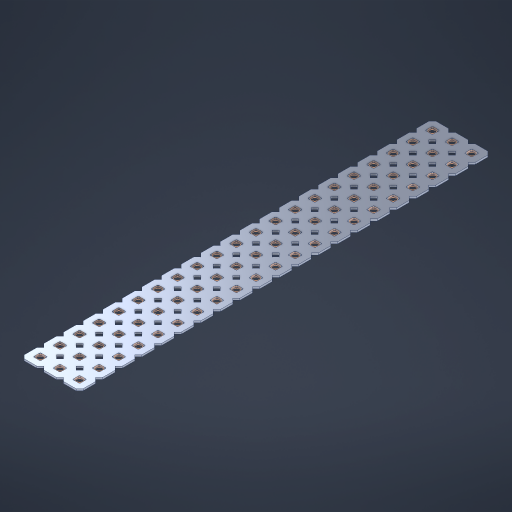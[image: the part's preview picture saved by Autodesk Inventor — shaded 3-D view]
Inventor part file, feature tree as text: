
AUTODESK INVENTOR PART (.ipt)
format: ipt  version: 2023 (Build 270158000, 158)  size: 988,160 bytes
history: native  units: in
note: dims shown in document units (in); Inventor stores cm internally (conversion verified against a paired STEP export)
features: other x64, extrude x62, sketch x2, pattern_linear x1
ambient origin geometry x8: Origin, YZ Plane, XZ Plane, XY Plane, X Axis, Y Axis, Z Axis, Center Point
bodies: Solid1 (feature_tree), Body (feature_tree)
feature tree (129):
  pattern_linear  "Rectangular Pattern1"  Spacing1=0.09in  [1 undecoded]
  sketch  "Sketch1"  dims[d1=0.5in]
  sketch  "Sketch2"  dims[d2=0.182in d3=0.09in d4=0.09in d5=0.09in d6=0.09in d7=0.09in d8=0.09in d9=0.09in d10=0.09in d11=0.02in d13=0.0in d14=0.172in d15=0.0625in d16=0.0in d19=0.5in d22=0.5in]
  other  "Srf1"
  other  "Srf126"
  other  "Srf127"
  other  "Srf128"
  other  "Srf129"
  other  "Srf130"
  other  "Srf131"
  other  "Srf250"
  other  "Srf251"
  other  "Srf252"
  other  "Srf253"
  other  "Srf254"
  other  "Srf255"
  other  "Srf256"
  other  "Srf257"
  other  "Srf258"
  other  "Srf259"
  other  "Srf260"
  other  "Srf261"
  other  "Srf262"
  other  "Srf263"
  other  "Srf268"
  other  "Srf269"
  other  "Srf270"
  other  "Srf271"
  other  "Srf272"
  other  "Srf273"
  other  "Srf274"
  other  "Srf275"
  other  "Srf276"
  other  "Srf277"
  other  "Srf278"
  other  "Srf279"
  other  "Srf280"
  other  "Srf281"
  other  "Srf282"
  other  "Srf283"
  other  "Srf284"
  other  "Srf285"
  other  "Srf286"
  other  "Srf287"
  other  "Srf288"
  other  "Srf293"
  other  "Srf294"
  other  "Srf295"
  other  "Srf296"
  other  "Srf297"
  other  "Srf298"
  other  "Srf299"
  other  "Srf300"
  other  "Srf301"
  other  "Srf302"
  other  "Srf303"
  other  "Srf304"
  other  "Srf305"
  other  "Srf306"
  other  "Srf307"
  other  "Srf308"
  other  "Srf309"
  other  "Srf310"
  other  "Srf311"
  other  "Srf312"
  other  "Srf313"
  other  "Circle"
  extrude  "ExtrusionSrf126"  Depth=0.09in
  extrude  "ExtrusionSrf127"  Depth=0.09in
  extrude  "ExtrusionSrf128"  Depth=0.09in
  extrude  "ExtrusionSrf129"  Depth=0.09in
  extrude  "ExtrusionSrf130"  Depth=0.09in
  extrude  "ExtrusionSrf131"  Depth=0.09in
  extrude  "ExtrusionSrf250"  Depth=0.09in
  extrude  "ExtrusionSrf251"  Depth=0.02in
  extrude  "ExtrusionSrf252"  TaperAngle=0.0deg  [1 undecoded]
  extrude  "ExtrusionSrf253"  Depth=0.5in
  extrude  "ExtrusionSrf254"  Depth=0.5in TaperAngle=0.0deg
  extrude  "ExtrusionSrf255"  Depth=0.5in
  extrude  "ExtrusionSrf256"  Depth=0.5in
  extrude  "ExtrusionSrf257"  [1 undecoded]
  extrude  "ExtrusionSrf258"  [1 undecoded]
  extrude  "ExtrusionSrf259"  [1 undecoded]
  extrude  "ExtrusionSrf260"  [1 undecoded]
  extrude  "ExtrusionSrf261"  [1 undecoded]
  extrude  "ExtrusionSrf262"  [1 undecoded]
  extrude  "ExtrusionSrf263"  [1 undecoded]
  extrude  "ExtrusionSrf268"  [1 undecoded]
  extrude  "ExtrusionSrf269"  [1 undecoded]
  extrude  "ExtrusionSrf270"  [1 undecoded]
  extrude  "ExtrusionSrf271"  [1 undecoded]
  extrude  "ExtrusionSrf272"  [1 undecoded]
  extrude  "ExtrusionSrf273"  [1 undecoded]
  extrude  "ExtrusionSrf274"  [1 undecoded]
  extrude  "ExtrusionSrf275"  [1 undecoded]
  extrude  "ExtrusionSrf276"  [1 undecoded]
  extrude  "ExtrusionSrf277"  [1 undecoded]
  extrude  "ExtrusionSrf278"  [1 undecoded]
  extrude  "ExtrusionSrf279"  [1 undecoded]
  extrude  "ExtrusionSrf280"  [1 undecoded]
  extrude  "ExtrusionSrf281"  [1 undecoded]
  extrude  "ExtrusionSrf282"  [1 undecoded]
  extrude  "ExtrusionSrf283"  [1 undecoded]
  extrude  "ExtrusionSrf284"  [1 undecoded]
  extrude  "ExtrusionSrf285"  [1 undecoded]
  extrude  "ExtrusionSrf286"  [1 undecoded]
  extrude  "ExtrusionSrf287"  [1 undecoded]
  extrude  "ExtrusionSrf288"  [1 undecoded]
  extrude  "ExtrusionSrf293"  [1 undecoded]
  extrude  "ExtrusionSrf294"  [1 undecoded]
  extrude  "ExtrusionSrf295"  [1 undecoded]
  extrude  "ExtrusionSrf296"  [1 undecoded]
  extrude  "ExtrusionSrf297"  [1 undecoded]
  extrude  "ExtrusionSrf298"  [1 undecoded]
  extrude  "ExtrusionSrf299"  [1 undecoded]
  extrude  "ExtrusionSrf300"  [1 undecoded]
  extrude  "ExtrusionSrf301"  [1 undecoded]
  extrude  "ExtrusionSrf302"  [1 undecoded]
  extrude  "ExtrusionSrf303"  [1 undecoded]
  extrude  "ExtrusionSrf304"  [1 undecoded]
  extrude  "ExtrusionSrf305"  [1 undecoded]
  extrude  "ExtrusionSrf306"  [1 undecoded]
  extrude  "ExtrusionSrf307"  [1 undecoded]
  extrude  "ExtrusionSrf308"  [1 undecoded]
  extrude  "ExtrusionSrf309"  [1 undecoded]
  extrude  "ExtrusionSrf310"  [1 undecoded]
  extrude  "ExtrusionSrf311"  [1 undecoded]
  extrude  "ExtrusionSrf312"  [1 undecoded]
  extrude  "ExtrusionSrf313"  [1 undecoded]
note: 51 required parameter values undecoded (feature->parameter linkage not recoverable at this tier; creation-order binding heuristic only, values carry confidence <= 0.55)
